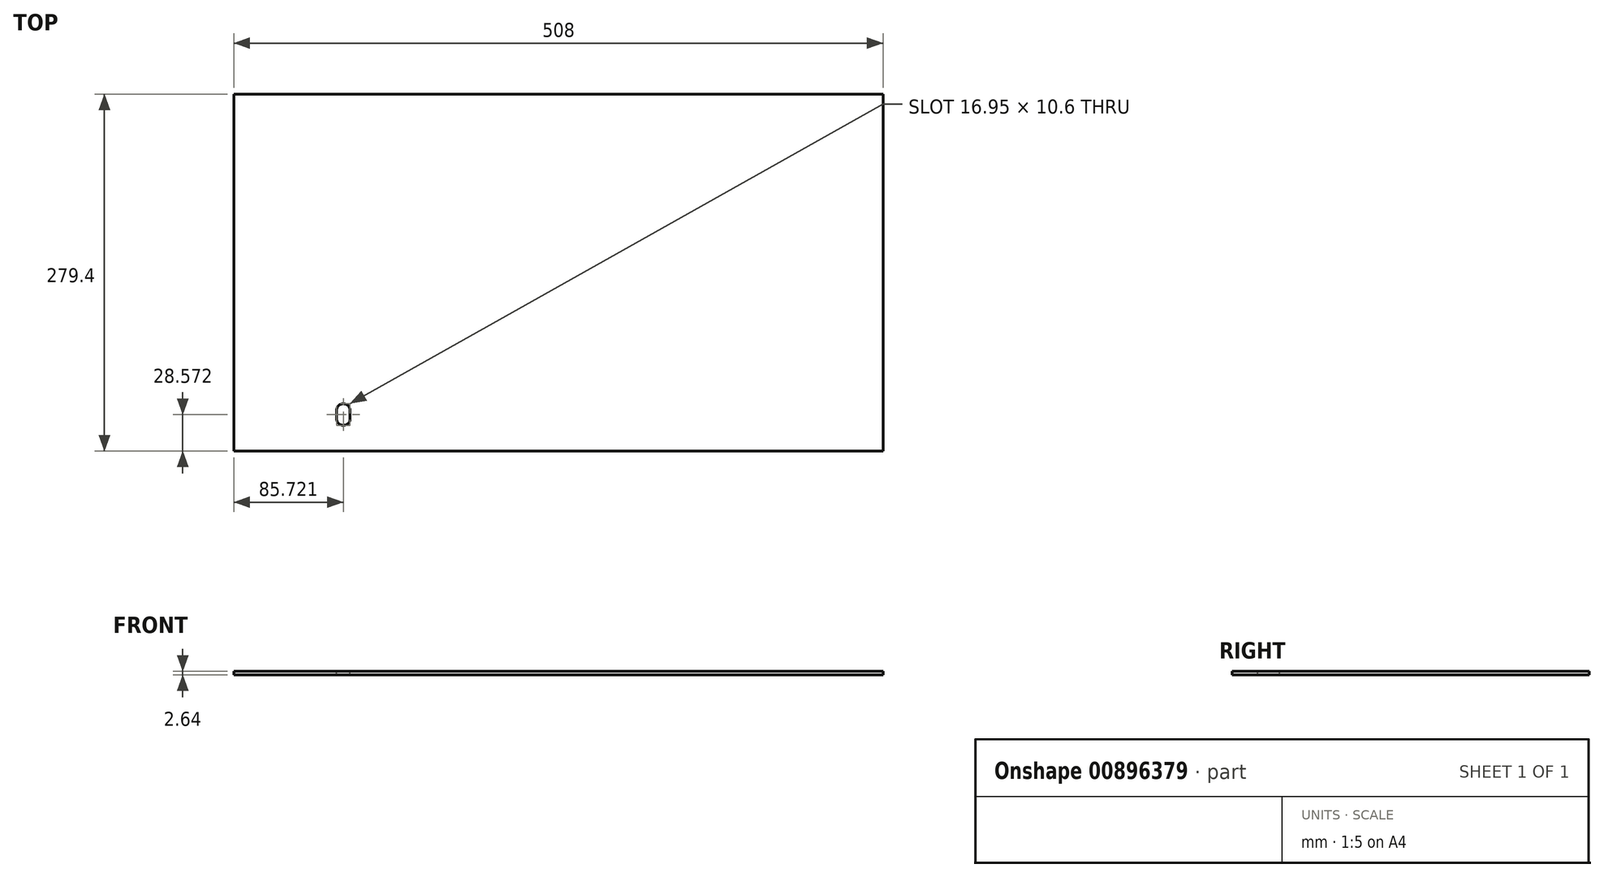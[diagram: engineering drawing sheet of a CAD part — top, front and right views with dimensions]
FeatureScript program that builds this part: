
annotation { "Feature Type Name" : "Feature", "Feature Type Description" : "" }
export const myFeature = defineFeature(function(context is Context, id is Id, definition is map)
    precondition{}
    {
        {
            var Q0;
            Q0=qCreatedBy(makeId("Top.planeOp"),FACE);
            var sketch = newSketch(context, id + "F0", { "sketchPlane" : qUnion([Q0])});
            skLineSegment(sketch, "E0.bottom", {"start": v(-273.76, 147.02) * mm, "end": v(234.24, 147.02) * mm});
            skLineSegment(sketch, "E0.top", {"start": v(-273.76, -132.38) * mm, "end": v(234.24, -132.38) * mm});
            skLineSegment(sketch, "E0.left", {"start": v(-273.76, 147.02) * mm, "end": v(-273.76, -132.38) * mm});
            skLineSegment(sketch, "E0.right", {"start": v(234.24, 147.02) * mm, "end": v(234.24, -132.38) * mm});
            skSolve(sketch);
        }
        {
            var Q0;
            Q0 = qSketchRegion(id + "F0", true);
            extrude(context, id + "F1", {"entities" : qUnion([Q0]), "depth" : 2.64 * mm, "offsetDistance" : 25.4 * mm});
        }
        {
            var Q0;
            Q0=makeQuery(id+"F1.opExtrude","CAP_FACE",FACE,{"disambiguationData":[OSD([sQuery(id+"F0.wireOp",EDGE,"E0.bottom"),sQuery(id+"F0.wireOp",EDGE,"E0.top"),sQuery(id+"F0.wireOp",EDGE,"E0.left"),sQuery(id+"F0.wireOp",EDGE,"E0.right")])],"isStart":false});
            var sketch = newSketch(context, id + "F2", { "sketchPlane" : qUnion([Q0])});
            skLineSegment(sketch, "E1", {"start": v(-188.04, -100.63) * mm, "end": v(-188.04, -106.98) * mm});
            skArc(sketch, "E2", {"start": v(-193.34, -106.98) * mm, "mid": v(-188.04, -112.28) * mm, "end": v(-182.74, -106.98) * mm});
            skLineSegment(sketch, "E3", {"start": v(-182.74, -106.98) * mm, "end": v(-182.74, -100.63) * mm});
            skLineSegment(sketch, "E4", {"start": v(-193.34, -106.98) * mm, "end": v(-193.34, -100.63) * mm});
            skArc(sketch, "E5", {"start": v(-182.74, -100.63) * mm, "mid": v(-188.04, -95.33) * mm, "end": v(-193.34, -100.63) * mm});
            skSolve(sketch);
        }
        {
            var Q0;
            Q0 = qSketchRegion(id + "F2", true);
            extrude(context, id + "F3", {"entities" : qUnion([Q0]), "operationType" : NewBodyOperationType.REMOVE, "oppositeDirection" : true, "depth" : 25.4 * mm, "offsetDistance" : 25.4 * mm});
        }
    });
